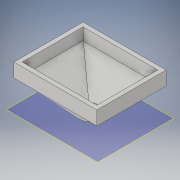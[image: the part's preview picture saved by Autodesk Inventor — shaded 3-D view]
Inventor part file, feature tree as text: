
AUTODESK INVENTOR PART (.ipt)
format: ipt  version: 2019 (Build 230136000, 136)  size: 223,744 bytes
history: native  units: in
note: dims shown in document units (in); Inventor stores cm internally (conversion verified against a paired STEP export)
features: sketch x3, extrude x1, plane x1, loft x1, shell x1, hole x1, other x1
ambient origin geometry x8: Origin, YZ Plane, XZ Plane, XY Plane, X Axis, Y Axis, Z Axis, Center Point
bodies: Solid1 (feature_tree)
feature tree (9):
  extrude  "Extrusion1"  Depth=2.9528in
  plane  "Work Plane1"
  loft  "Loft1"
  shell  "Shell1"  Thickness=9.8425in
  hole  "Hole1"  [1 undecoded]
  sketch  "Sketch1"  dims[d0=11.811in d1=2.9528in]
  sketch  "Sketch2"  dims[d2=1.9685in d3=5.9055in d4=9.8425in d5=0.0in]
  other  "Edges1"
  sketch  "Sketch3"  dims[d6=3.937in d7=2.7559in d8=4.9213in d9=5.9055in d10=0.0in d11=90.0deg d12=0.0in d13=90.0deg d14=0.5906in d15=2.7559in d16=0.2362in d17=0.1575in d18=0.0787in d19=90.0deg d20=0.3543in d21=0.8108in d22=0.0295in d23=0.8108in d24=0.0025in d25=0.0295in d26=0.0148in]
note: 1 required parameter value undecoded (feature->parameter linkage not recoverable at this tier; creation-order binding heuristic only, values carry confidence <= 0.55)
